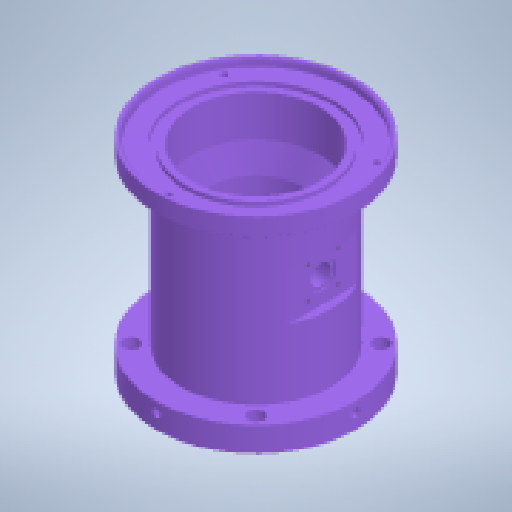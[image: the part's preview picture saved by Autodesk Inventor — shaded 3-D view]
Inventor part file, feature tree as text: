
AUTODESK INVENTOR PART (.ipt)
format: ipt  version: 2023 (Build 270158000, 158)  size: 563,200 bytes
history: native  units: mm
features: sketch x17, extrude x8, hole x7, pattern_circular x5, projected_geometry x5, plane x3, other x3, revolve x2, chamfer x2, reference x1
ambient origin geometry x8: Origin, YZ Plane, XZ Plane, XY Plane, X Axis, Y Axis, Z Axis, Center Point
bodies: Solid1 (feature_tree)
feature tree (53):
  revolve  "Revolution1"  [1 undecoded]
  revolve  "Revolution2"  Angle=360.0deg
  plane  "Work Plane1"
  hole  "Hole1"  [1 undecoded]
  pattern_circular  "Circular Pattern1"  Count=7  [1 undecoded]
  hole  "Hole4"  [1 undecoded]
  pattern_circular  "Circular Pattern3"  [2 undecoded]
  hole  "Hole5"  [1 undecoded]
  pattern_circular  "Circular Pattern4"  [2 undecoded]
  extrude  "Extrusion2"  Depth=10.0mm TaperAngle=360.0deg
  plane  "Work Plane4"
  extrude  "Extrusion4"  Depth=10.0mm
  extrude  "Extrusion5"  TaperAngle=45.0deg  [1 undecoded]
  extrude  "Extrusion1"  Depth=10.0mm TaperAngle=360.0deg
  extrude  "Extrusion6"  Depth=10.0mm
  hole  "Hole6"  [1 undecoded]
  plane  "Work Plane5"
  extrude  "Extrusion7"  Depth=10.0mm
  extrude  "Extrusion8"  Depth=10.0mm
  extrude  "Extrusion9"  TaperAngle=135.0deg  [1 undecoded]
  hole  "Hole7"  [1 undecoded]
  chamfer  "Chamfer1"  Distance=10.5mm
  hole  "Hole8"  [1 undecoded]
  pattern_circular  "Circular Pattern5"  Count=12  [1 undecoded]
  hole  "Hole9"  [1 undecoded]
  pattern_circular  "Circular Pattern6"  [2 undecoded]
  chamfer  "Chamfer2"  Angle=135.0deg  [1 undecoded]
  sketch  "Sketch1"  dims[d14=360.0deg d17=36.0mm]
  sketch  "Sketch2"  dims[d28=14.5mm]
  sketch  "Sketch3"  dims[d30=3.242mm d31=42.0mm d32=5.0mm d33=20.0mm d34=90.0deg d35=40.0mm d36=20.594885mm d37=40.0mm d38=360.0deg]
  sketch  "Sketch7"  dims[d40=70.0mm d42=28.0mm]
  sketch  "Sketch8"  dims[d43=4.0mm d44=0.0mm]
  sketch  "Sketch9"  dims[d70=38.0mm]
  projected_geometry  "Projected Loop1"
  projected_geometry  "Projected Loop2"
  sketch  "Sketch10"  dims[d71=2.0mm]
  projected_geometry  "Projected Loop3"
  sketch  "Sketch13"  dims[d72=1.0mm]
  sketch  "Sketch14"  dims[d73=8.0mm]
  projected_geometry  "Projected Loop5"
  sketch  "Sketch16"  dims[d74=3.0mm]
  sketch  "Sketch17"  dims[d75=2.0mm]
  sketch  "Sketch18"  dims[d76=55.0mm d77=70.0mm]
  reference  "Reference1"
  sketch  "Sketch19"  dims[d78=4.0mm d80=120.0mm]
  projected_geometry  "Projected Loop7"
  sketch  "Sketch20"  dims[d81=82.9mm]
  sketch  "Sketch21"  dims[d82=2.0mm]
  sketch  "Sketch22"  dims[d83=82.9mm]
  sketch  "Sketch23"  dims[d84=12.0mm d86=23.0mm d87=1.567mm d88=4.0mm d89=6.3mm d90=2.0mm d91=90.0deg d92=6.0mm d93=20.594885mm d94=135.0deg d95=6.0mm d96=40.0mm d97=360.0deg d99=53.0mm d100=45.0deg d101=10.0mm d102=6.0mm d103=17.3mm d104=2.0mm d105=90.0deg d106=8.0mm d107=0.0mm d108=40.0mm d109=360.0deg d111=27.925268mm d112=78.0mm d113=2.0mm d114=90.0mm d115=135.0deg d117=100.8mm d118=10.5mm d119=2.0mm d120=120.0mm d121=77.0mm d122=114.0mm d123=135.0deg d124=6.0mm d125=3.5mm d126=2.5mm d127=85.0mm d128=360.0deg d129=3.0mm d130=3.0mm d131=0.0mm d132=65.0mm d139=12.0mm d140=0.0mm d142=65.0mm d143=40.0mm d144=20.0mm d145=0.0mm d150=2.0mm d152=1.0mm d153=0.0mm d154=59.5mm d156=54.0mm d157=2.459mm d158=6.0mm d159=4.0mm d160=2.0mm d161=90.0deg d162=8.8mm d163=20.594885mm d164=135.0deg d165=0.0mm d166=30.0mm d167=5.0mm d168=0.0mm d169=12.0mm d170=15.0mm d171=0.0mm d172=2.0mm d173=1.0mm d174=0.0mm d175=29.5mm d176=26.0mm d177=2.459mm d178=6.0mm d179=4.0mm d180=2.0mm d181=90.0deg d182=8.8mm d183=20.594885mm d184=5.0mm d185=2.0mm d186=45.0deg d187=53.0mm d188=3.6mm d189=6.0mm d190=6.3mm d191=2.0mm d192=90.0deg d193=8.8mm d194=20.594885mm d195=30.0mm d196=360.0deg d198=4.0mm d199=0.0mm d200=106.0mm d201=9.0mm d202=6.0mm d203=17.3mm d204=2.0mm d205=90.0deg d206=8.8mm d207=20.594885mm d208=40.0mm d209=360.0deg d211=0.25mm d212=2.0mm d213=45.0deg]
  parser-record x1  (decoder bookkeeping rows leaked as tree rows — omitted from the tree; the rows remain in map.json)
  other  "AnodeHousing.iam"
  other  "AnodeHolder:1"
note: 19 required parameter values undecoded (feature->parameter linkage not recoverable at this tier; creation-order binding heuristic only, values carry confidence <= 0.55)
note: 1 file-system path scrubbed to <path> (originals preserved in map.json)